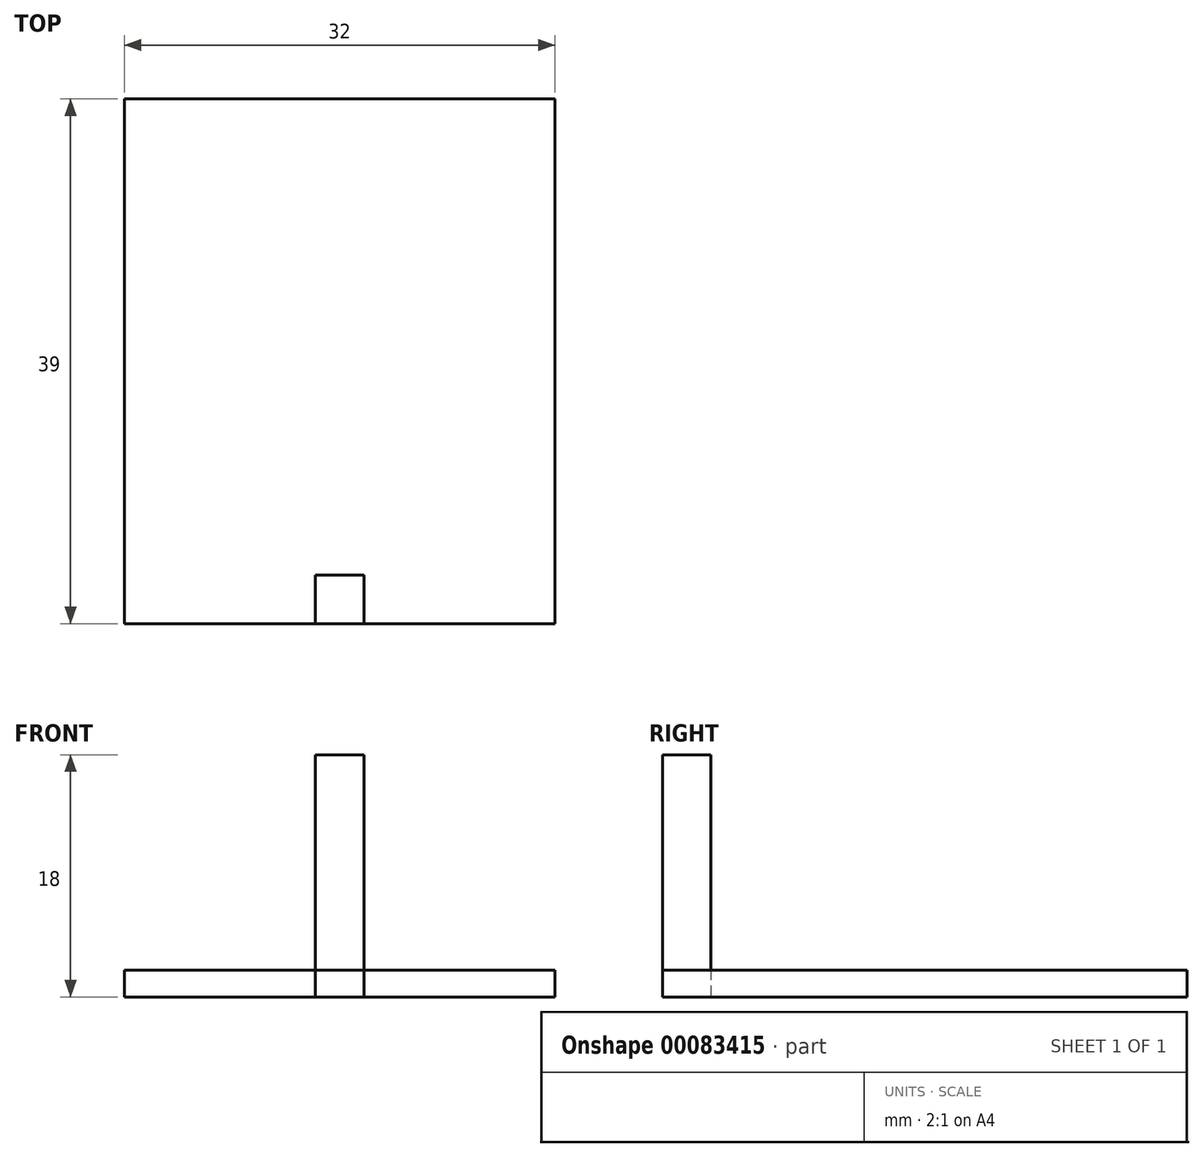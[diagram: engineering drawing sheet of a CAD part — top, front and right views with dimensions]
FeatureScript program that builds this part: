
annotation { "Feature Type Name" : "Feature", "Feature Type Description" : "" }
export const myFeature = defineFeature(function(context is Context, id is Id, definition is map)
    precondition{}
    {
        {
            var Q0;
            Q0=qCreatedBy(makeId("Top.planeOp"),FACE);
            var sketch = newSketch(context, id + "F0", { "sketchPlane" : qUnion([Q0])});
            skLineSegment(sketch, "E0.bottom", {"start": v(0, 0) * mm, "end": v(32, 0) * mm});
            skLineSegment(sketch, "E0.top", {"start": v(0, 39) * mm, "end": v(32, 39) * mm});
            skLineSegment(sketch, "E0.left", {"start": v(0, 0) * mm, "end": v(0, 39) * mm});
            skLineSegment(sketch, "E0.right", {"start": v(32, 0) * mm, "end": v(32, 39) * mm});
            skLineSegment(sketch, "E1", {"start": v(16, 0) * mm, "end": v(16, 3.6) * mm});
            skLineSegment(sketch, "E2", {"start": v(16, 3.6) * mm, "end": v(17.8, 3.6) * mm});
            skLineSegment(sketch, "E3", {"start": v(17.8, 3.6) * mm, "end": v(17.8, 0) * mm});
            skLineSegment(sketch, "E4", {"start": v(16, 3.6) * mm, "end": v(14.2, 3.6) * mm});
            skLineSegment(sketch, "E5", {"start": v(14.2, 3.6) * mm, "end": v(14.2, 0) * mm});
            skSolve(sketch);
        }
        {
            var Q0;
            Q0=makeQuery(id+"F0.imprint","IMPRINT",FACE,{"disambiguationData":[TD([[makeQuery(id+"F0.imprint","IMPRINT",EDGE,{"derivedFrom":sQuery(id+"F0.wireOp",EDGE,"E0.top")}),-1.0]])]});
            var Q1;
            {var subQ0=sQuery(id+"F0.wireOp",EDGE,"E1");Q1=makeQuery(id+"F0.imprint","IMPRINT",FACE,{"disambiguationData":[TD([[makeQuery(id+"F0.imprint","IMPRINT",EDGE,{"derivedFrom":subQ0}),1.0]])]});}
            var Q2;
            {var subQ0=sQuery(id+"F0.wireOp",EDGE,"E1");Q2=makeQuery(id+"F0.imprint","IMPRINT",FACE,{"disambiguationData":[TD([[makeQuery(id+"F0.imprint","IMPRINT",EDGE,{"derivedFrom":subQ0}),-1.0]])]});}
            extrude(context, id + "F1", {"entities" : qUnion([Q0, Q1, Q2]), "offsetDistance" : 25 * mm, "depth" : 2 * mm});
        }
        {
            var Q0;
            {var subQ0=sQuery(id+"F0.wireOp",EDGE,"E1");Q0=makeQuery(id+"F0.imprint","IMPRINT",FACE,{"disambiguationData":[TD([[makeQuery(id+"F0.imprint","IMPRINT",EDGE,{"derivedFrom":subQ0}),1.0]])]});}
            var Q1;
            {var subQ0=sQuery(id+"F0.wireOp",EDGE,"E1");Q1=makeQuery(id+"F0.imprint","IMPRINT",FACE,{"disambiguationData":[TD([[makeQuery(id+"F0.imprint","IMPRINT",EDGE,{"derivedFrom":subQ0}),-1.0]])]});}
            extrude(context, id + "F2", {"entities" : qUnion([Q0, Q1]), "offsetDistance" : 25 * mm, "depth" : 18 * mm});
        }
    });
